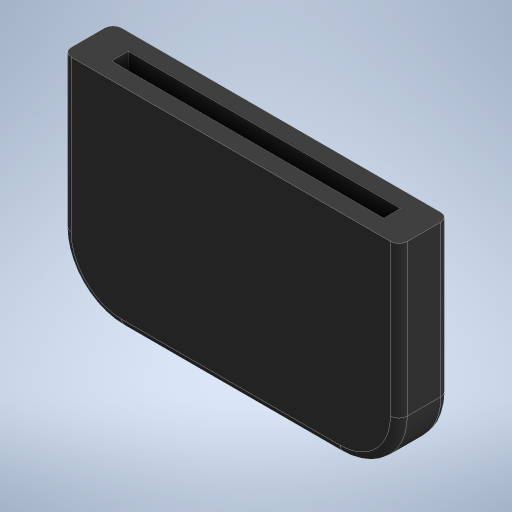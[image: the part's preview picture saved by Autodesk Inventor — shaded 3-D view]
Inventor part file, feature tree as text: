
AUTODESK INVENTOR PART (.ipt)
format: ipt  version: 2024 (Build 280153000, 153)  size: 314,880 bytes
history: native  units: mm
features: fillet x4, extrude x3, sketch x3, projected_geometry x2, mirror x1, other x1
ambient origin geometry x8: Origin, YZ Plane, XZ Plane, XY Plane, X Axis, Y Axis, Z Axis, Center Point
bodies: Solid3 (feature_tree)
feature tree (14):
  extrude  "Extrusion5"  Depth=21.0mm
  fillet  "Fillet2"  Radius=7.0mm
  fillet  "Fillet3"  Radius=9.0mm
  fillet  "Fillet4"  Radius=5.0mm
  extrude  "Extrusion6"  Depth=1.0mm
  extrude  "Extrusion7"  Depth=1.0mm
  mirror  "Mirror1"
  fillet  "Fillet5"  Radius=0.2mm
  sketch  "Sketch3"  dims[d24=32.0mm d25=21.0mm d26=7.0mm d27=9.0mm d28=5.0mm]
  sketch  "Sketch4"  dims[d29=1.6mm d30=0.0mm d31=1.0mm]
  other  "Bumper"
  sketch  "Sketch5"  dims[d32=3.0mm d33=1.0mm d34=0.2mm d35=4.0mm d36=2.0mm d37=0.0mm d38=2.0mm d39=0.0mm d40=1.0mm]
  projected_geometry  "Projected Loop1"
  projected_geometry  "Project Cut Edges1"
